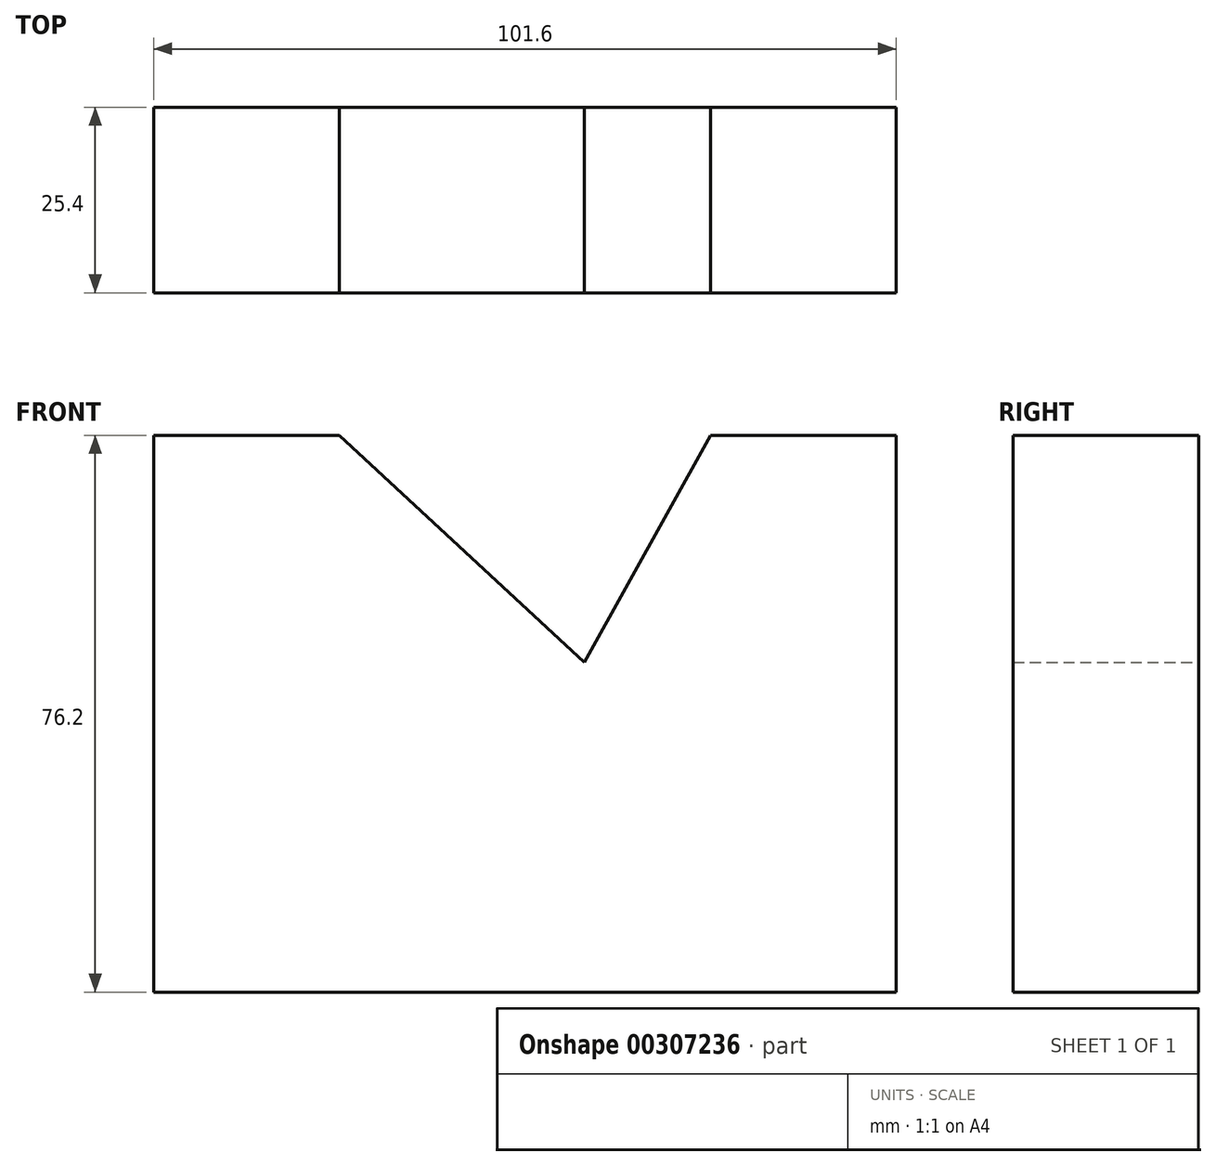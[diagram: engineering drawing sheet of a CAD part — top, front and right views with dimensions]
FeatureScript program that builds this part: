
annotation { "Feature Type Name" : "Feature", "Feature Type Description" : "" }
export const myFeature = defineFeature(function(context is Context, id is Id, definition is map)
    precondition{}
    {
        {
            var Q0;
            Q0=qCreatedBy(makeId("Front.planeOp"),FACE);
            var sketch = newSketch(context, id + "F0", { "sketchPlane" : qUnion([Q0])});
            skLineSegment(sketch, "E0", {"start": v(-37.83, 60.92) * mm, "end": v(-63.23, 60.92) * mm});
            skLineSegment(sketch, "E1", {"start": v(-63.23, 60.92) * mm, "end": v(-63.23, -15.28) * mm});
            skLineSegment(sketch, "E2", {"start": v(-63.23, -15.28) * mm, "end": v(38.37, -15.28) * mm});
            skLineSegment(sketch, "E3", {"start": v(38.37, -15.28) * mm, "end": v(38.37, 60.92) * mm});
            skLineSegment(sketch, "E4", {"start": v(38.37, 60.92) * mm, "end": v(12.97, 60.92) * mm});
            skLineSegment(sketch, "E5", {"start": v(12.97, 60.92) * mm, "end": v(-4.3, 29.84) * mm});
            skLineSegment(sketch, "E6", {"start": v(-4.3, 29.84) * mm, "end": v(-37.83, 60.92) * mm});
            skSolve(sketch);
        }
        {
            var Q0;
            Q0 = qSketchRegion(id + "F0", true);
            extrude(context, id + "F1", {"entities" : qUnion([Q0]), "depth" : 25.4 * mm});
        }
    });
